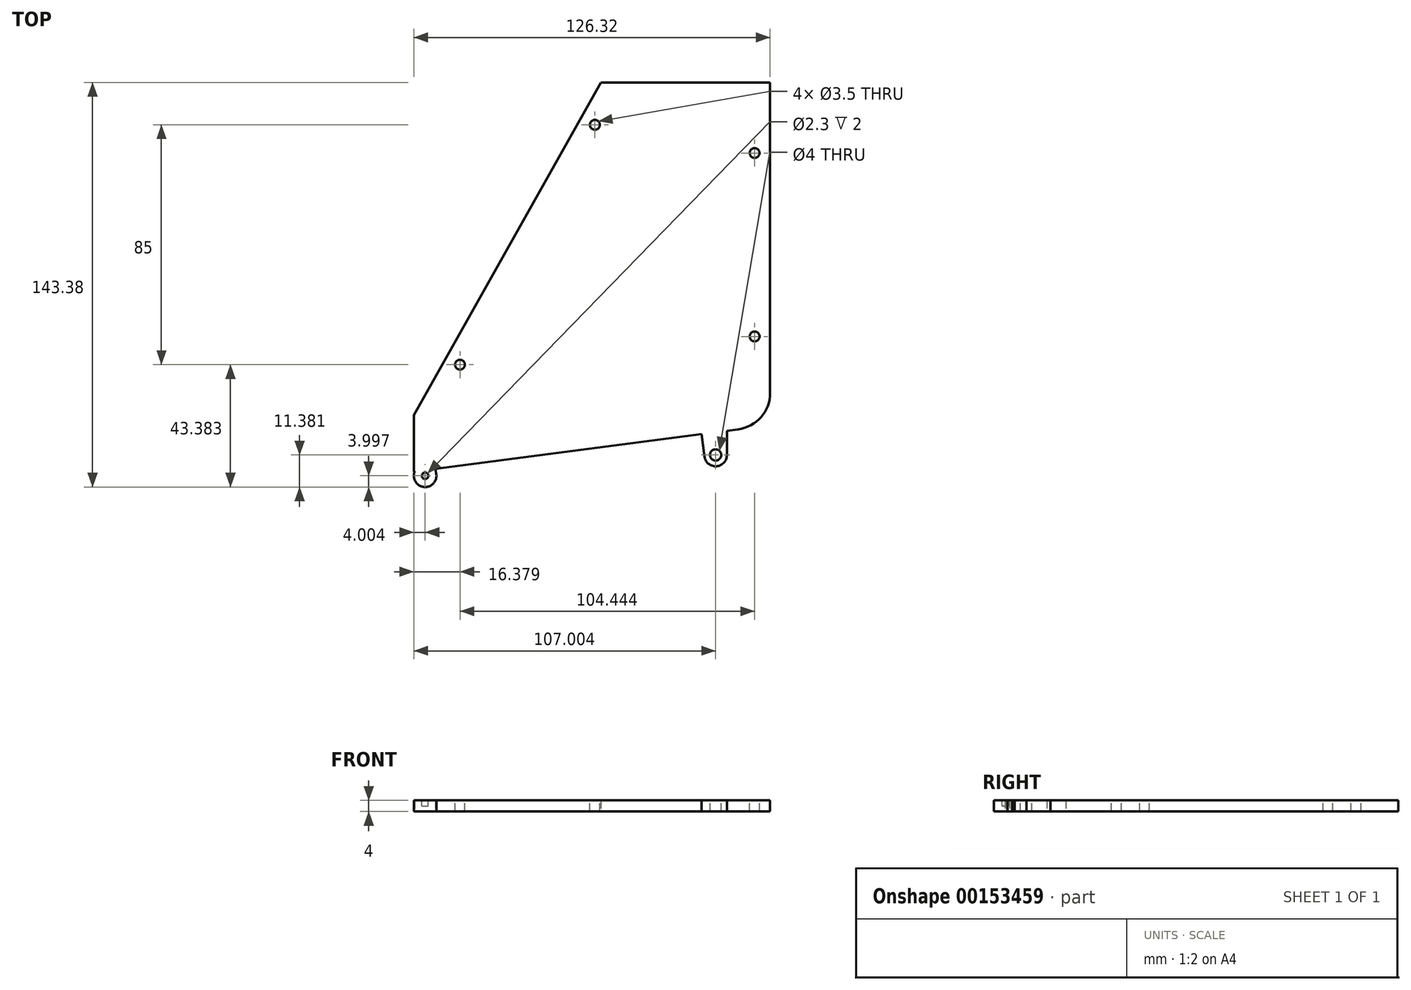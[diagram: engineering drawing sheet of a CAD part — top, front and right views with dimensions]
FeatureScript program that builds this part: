
annotation { "Feature Type Name" : "Feature", "Feature Type Description" : "" }
export const myFeature = defineFeature(function(context is Context, id is Id, definition is map)
    precondition{}
    {
        {
            var Q0;
            Q0=qCreatedBy(makeId("Top.planeOp"),FACE);
            var sketch = newSketch(context, id + "F0", { "sketchPlane" : qUnion([Q0])});
            skLineSegment(sketch, "E0", {"start": v(-60.03, 83.64) * mm, "end": v(-60.03, -26.36) * mm});
            skLineSegment(sketch, "E1", {"start": v(-48.72, -39.25) * mm, "end": v(66.28, -54.25) * mm});
            skLineSegment(sketch, "E2", {"start": v(66.28, -34.25) * mm, "end": v(-0.03, 83.64) * mm});
            skLineSegment(sketch, "E3", {"start": v(-60.03, 83.64) * mm, "end": v(-0.03, 83.64) * mm});
            skLineSegment(sketch, "E4", {"start": v(66.28, -34.25) * mm, "end": v(66.28, -54.25) * mm});
            skPoint(sketch, "E5.visualSharp", {"position": v(-60.03, -37.77) * mm});
            skArc(sketch, "E5.filletArc", {"start": v(-60.03, -26.36) * mm, "mid": v(-56.8, -34.93) * mm, "end": v(-48.72, -39.25) * mm});
            skCircle(sketch, "E6", {"center": v(62.28, -55.74) * mm, "radius": 4 * mm});
            skLineSegment(sketch, "E7", {"start": v(66.28, -55.79) * mm, "end": v(66.28, -54.25) * mm});
            skLineSegment(sketch, "E8", {"start": v(58.37, -54.91) * mm, "end": v(58.59, -53.24) * mm});
            skCircle(sketch, "E9", {"center": v(-40.72, -48.36) * mm, "radius": 4 * mm});
            skLineSegment(sketch, "E10", {"start": v(-44.71, -48.48) * mm, "end": v(-44.71, -39.77) * mm});
            skLineSegment(sketch, "E11", {"start": v(-36.75, -48.88) * mm, "end": v(-35.72, -40.94) * mm});
            skSolve(sketch);
        }
        {
            var Q0;
            {var subQ0=sQuery(id+"F0.wireOp",EDGE,"E7");var subQ1=sQuery(id+"F0.wireOp",EDGE,"E6");var subQ2=makeQuery(id+"F0.imprint","INTERSECT",VERTEX,{"disambiguationData":[OD(0.0)],"derivedFrom":[subQ1,subQ0]});Q0=makeQuery(id+"F0.imprint","IMPRINT",FACE,{"disambiguationData":[TD([[makeQuery(id+"F0.imprint","IMPRINT",EDGE,{"disambiguationData":[TD([[subQ2,-1.0]])],"derivedFrom":subQ1}),1.0]])]});}
            var Q1;
            {var subQ0=sQuery(id+"F0.wireOp",EDGE,"E10");var subQ1=sQuery(id+"F0.wireOp",EDGE,"E9");var subQ2=makeQuery(id+"F0.imprint","INTERSECT",VERTEX,{"disambiguationData":[OD(0.0)],"derivedFrom":[subQ1,subQ0]});Q1=makeQuery(id+"F0.imprint","IMPRINT",FACE,{"disambiguationData":[TD([[makeQuery(id+"F0.imprint","IMPRINT",EDGE,{"disambiguationData":[TD([[subQ2,1.0]])],"derivedFrom":subQ1}),1.0]])]});}
            var Q2;
            {var subQ0=sQuery(id+"F0.wireOp",EDGE,"E10");var subQ1=sQuery(id+"F0.wireOp",EDGE,"E1");var subQ2=makeQuery(id+"F0.imprint","INTERSECT",VERTEX,{"derivedFrom":[subQ1,subQ0]});Q2=makeQuery(id+"F0.imprint","IMPRINT",FACE,{"disambiguationData":[TD([[makeQuery(id+"F0.imprint","IMPRINT",EDGE,{"disambiguationData":[TD([[subQ2,-1.0]])],"derivedFrom":subQ1}),-1.0]])]});}
            var Q3;
            {var subQ0=sQuery(id+"F0.wireOp",EDGE,"E11");Q3=makeQuery(id+"F0.imprint","IMPRINT",FACE,{"disambiguationData":[TD([[makeQuery(id+"F0.imprint","IMPRINT",EDGE,{"derivedFrom":subQ0}),1.0]])]});}
            var Q4;
            {var subQ0=sQuery(id+"F0.wireOp",EDGE,"E8");Q4=makeQuery(id+"F0.imprint","IMPRINT",FACE,{"disambiguationData":[TD([[makeQuery(id+"F0.imprint","IMPRINT",EDGE,{"derivedFrom":subQ0}),-1.0]])]});}
            var Q5;
            {var subQ0=sQuery(id+"F0.wireOp",EDGE,"E7");var subQ3=sQuery(id+"F0.wireOp",EDGE,"E6");var subQ5=makeQuery(id+"F0.imprint","INTERSECT",VERTEX,{"disambiguationData":[OD(1.0)],"derivedFrom":[subQ3,subQ0]});Q5=makeQuery(id+"F0.imprint","IMPRINT",FACE,{"disambiguationData":[TD([[makeQuery(id+"F0.imprint","IMPRINT",EDGE,{"disambiguationData":[TD([[subQ5,-1.0]])],"derivedFrom":subQ3}),-1.0]])]});}
            var Q6;
            {var subQ0=sQuery(id+"F0.wireOp",EDGE,"E9");var subQ2=sQuery(id+"F0.wireOp",EDGE,"E1");var subQ7=makeQuery(id+"F0.imprint","INTERSECT",VERTEX,{"disambiguationData":[OD(0.0)],"derivedFrom":[subQ2,subQ0]});Q6=makeQuery(id+"F0.imprint","IMPRINT",FACE,{"disambiguationData":[TD([[makeQuery(id+"F0.imprint","IMPRINT",EDGE,{"disambiguationData":[TD([[subQ7,-1.0]])],"derivedFrom":subQ2}),-1.0]])]});}
            var Q7;
            {var subQ1=sQuery(id+"F0.wireOp",EDGE,"E6");var subQ4=sQuery(id+"F0.wireOp",EDGE,"E1");var subQ5=makeQuery(id+"F0.imprint","INTERSECT",VERTEX,{"disambiguationData":[OD(0.0)],"derivedFrom":[subQ4,subQ1]});Q7=makeQuery(id+"F0.imprint","IMPRINT",FACE,{"disambiguationData":[TD([[makeQuery(id+"F0.imprint","IMPRINT",EDGE,{"disambiguationData":[TD([[subQ5,-1.0]])],"derivedFrom":subQ4}),-1.0]])]});}
            var Q8;
            {var subQ0=sQuery(id+"F0.wireOp",EDGE,"E6");var subQ1=sQuery(id+"F0.wireOp",EDGE,"E1");var subQ2=makeQuery(id+"F0.imprint","INTERSECT",VERTEX,{"disambiguationData":[OD(0.0)],"derivedFrom":[subQ1,subQ0]});Q8=makeQuery(id+"F0.imprint","IMPRINT",FACE,{"disambiguationData":[TD([[makeQuery(id+"F0.imprint","IMPRINT",EDGE,{"disambiguationData":[TD([[subQ2,-1.0]])],"derivedFrom":subQ1}),1.0]])]});}
            var Q9;
            Q9=makeQuery(id+"F0.imprint","IMPRINT",FACE,{"disambiguationData":[TD([[makeQuery(id+"F0.imprint","IMPRINT",EDGE,{"derivedFrom":sQuery(id+"F0.wireOp",EDGE,"E0")}),1.0]])]});
            var Q10;
            {var subQ0=sQuery(id+"F0.wireOp",EDGE,"E9");var subQ1=sQuery(id+"F0.wireOp",EDGE,"E1");var subQ2=makeQuery(id+"F0.imprint","INTERSECT",VERTEX,{"disambiguationData":[OD(0.0)],"derivedFrom":[subQ1,subQ0]});Q10=makeQuery(id+"F0.imprint","IMPRINT",FACE,{"disambiguationData":[TD([[makeQuery(id+"F0.imprint","IMPRINT",EDGE,{"disambiguationData":[TD([[subQ2,-1.0]])],"derivedFrom":subQ1}),1.0]])]});}
            var Q11;
            {var subQ0=sQuery(id+"F0.wireOp",EDGE,"E10");var subQ1=sQuery(id+"F0.wireOp",EDGE,"E9");var subQ2=makeQuery(id+"F0.imprint","INTERSECT",VERTEX,{"disambiguationData":[OD(0.0)],"derivedFrom":[subQ1,subQ0]});Q11=makeQuery(id+"F0.imprint","IMPRINT",FACE,{"disambiguationData":[TD([[makeQuery(id+"F0.imprint","IMPRINT",EDGE,{"disambiguationData":[TD([[subQ2,-1.0]])],"derivedFrom":subQ1}),1.0]])]});}
            extrude(context, id + "F1", {"entities" : qUnion([Q0, Q1, Q2, Q3, Q4, Q5, Q6, Q7, Q8, Q9, Q10, Q11]), "depth" : 4 * mm});
        }
        {
            var Q0;
            Q0=makeQuery(id+"F1.opExtrude","CAP_FACE",FACE,{"disambiguationData":[OSD([sQuery(id+"F0.wireOp",EDGE,"E0"),sQuery(id+"F0.wireOp",EDGE,"E1"),sQuery(id+"F0.wireOp",EDGE,"E2"),sQuery(id+"F0.wireOp",EDGE,"E3"),sQuery(id+"F0.wireOp",EDGE,"E4"),sQuery(id+"F0.wireOp",EDGE,"E5.filletArc")])],"isStart":false});
            var sketch = newSketch(context, id + "F2", { "sketchPlane" : qUnion([Q0])});
            skLineSegment(sketch, "E12.0", {"start": v(-48.46, -37.26) * mm, "end": v(52.4, -50.42) * mm});
            skArc(sketch, "E12.1", {"start": v(-58.03, -26.36) * mm, "mid": v(-55.3, -33.61) * mm, "end": v(-48.46, -37.26) * mm});
            skLineSegment(sketch, "E12.2", {"start": v(-58.03, 83.64) * mm, "end": v(-58.03, -26.36) * mm});
            skLineSegment(sketch, "E13", {"start": v(66.28, -54.25) * mm, "end": v(66.28, -52.23) * mm});
            skLineSegment(sketch, "E14", {"start": v(-60.03, 83.64) * mm, "end": v(-58.03, 83.64) * mm});
            skLineSegment(sketch, "E15", {"start": v(-48.46, -37.26) * mm, "end": v(-48.72, -39.25) * mm});
            skLineSegment(sketch, "E16.0", {"start": v(59.2, -25.73) * mm, "end": v(-2.7, 84.31) * mm});
            skLineSegment(sketch, "E17", {"start": v(-2.33, 83.64) * mm, "end": v(-2.7, 84.31) * mm});
            skLineSegment(sketch, "E18", {"start": v(59.2, -25.73) * mm, "end": v(66.28, -34.25) * mm});
            skSolve(sketch);
        }
        {
            var Q0;
            Q0=qSketchRegion(id+"F2",true);
            var Q1;
            Q1=makeQuery(id+"F2.imprint","IMPRINT",FACE,{"disambiguationData":[TD([[makeQuery(id+"F2.imprint","IMPRINT",EDGE,{"derivedFrom":sQuery(id+"F2.wireOp",EDGE,"E12.1")}),-1.0]])]});
            var Q2;
            {var subQ2=sQuery(id+"F2.wireOp",EDGE,"E17");Q2=makeQuery(id+"F2.imprint","IMPRINT",FACE,{"disambiguationData":[TD([[makeQuery(id+"F2.imprint","IMPRINT",EDGE,{"derivedFrom":subQ2}),-1.0]])]});}
            var Q3;
            {var subQ0=sQuery(id+"F2.wireOp",EDGE,"E16.0");Q3=makeQuery(id+"F2.imprint","IMPRINT",FACE,{"disambiguationData":[TD([[makeQuery(id+"F2.imprint","IMPRINT",EDGE,{"derivedFrom":subQ0}),-1.0]])]});}
            extrude(context, id + "F3", {"entities" : qUnion([Q0, Q1, Q2, Q3]), "operationType" : NewBodyOperationType.ADD, "depth" : 55 * mm});
        }
        {
            var Q0;
            {var subQ0=sQuery(id+"F0.wireOp",EDGE,"E0");Q0=makeQuery(id+"F3.boolean.opBoolean","MERGE",FACE,{"derivedFrom":[makeQuery(id+"F1.opExtrude","SWEPT_FACE",FACE,{"disambiguationData":[OSD([subQ0])]}),makeQuery(id+"F3.opExtrude","SWEPT_FACE",FACE,{"disambiguationData":[OSD([subQ0])]})]});}
            var sketch = newSketch(context, id + "F4", { "sketchPlane" : qUnion([Q0])});
            skCircle(sketch, "E19", {"center": v(23.36, 41.5) * mm, "radius": 2.5 * mm});
            skCircle(sketch, "E20", {"center": v(-74.64, 41.5) * mm, "radius": 2.5 * mm});
            skSolve(sketch);
        }
        {
            var Q0;
            Q0=qSketchRegion(id+"F4",true);
            extrude(context, id + "F5", {"entities" : qUnion([Q0]), "operationType" : NewBodyOperationType.REMOVE, "endBound" : BoundingType.UP_TO_NEXT, "oppositeDirection" : true, "depth" : 25 * mm});
        }
        {
            var Q0;
            Q0=makeQuery(id+"F1.opExtrude","CAP_FACE",FACE,{"disambiguationData":[OSD([sQuery(id+"F0.wireOp",EDGE,"E0"),sQuery(id+"F0.wireOp",EDGE,"E1"),sQuery(id+"F0.wireOp",EDGE,"E2"),sQuery(id+"F0.wireOp",EDGE,"E3"),sQuery(id+"F0.wireOp",EDGE,"E4"),sQuery(id+"F0.wireOp",EDGE,"E5.filletArc"),sQuery(id+"F0.wireOp",EDGE,"E6"),sQuery(id+"F0.wireOp",EDGE,"E7"),sQuery(id+"F0.wireOp",EDGE,"E8")])],"isStart":false});
            var sketch = newSketch(context, id + "F6", { "sketchPlane" : qUnion([Q0])});
            skCircle(sketch, "E21", {"center": v(62.28, -55.74) * mm, "radius": 1.15 * mm});
            skSolve(sketch);
        }
        {
            var Q0;
            Q0=qSketchRegion(id+"F6",true);
            extrude(context, id + "F7", {"entities" : qUnion([Q0]), "operationType" : NewBodyOperationType.REMOVE, "oppositeDirection" : true, "depth" : 2 * mm});
        }
        {
            var Q0;
            Q0=makeQuery(id+"F3.opExtrude","CAP_FACE",FACE,{"disambiguationData":[OSD([sQuery(id+"F0.wireOp",EDGE,"E0"),sQuery(id+"F0.wireOp",EDGE,"E5.filletArc"),sQuery(id+"F2.wireOp",EDGE,"E12.1"),sQuery(id+"F2.wireOp",EDGE,"E12.2"),sQuery(id+"F2.wireOp",EDGE,"E14"),sQuery(id+"F2.wireOp",EDGE,"E15")])],"isStart":false});
            var sketch = newSketch(context, id + "F8", { "sketchPlane" : qUnion([Q0])});
            skCircle(sketch, "E22", {"center": v(-54.53, -6.36) * mm, "radius": 3.5 * mm});
            skLineSegment(sketch, "E23", {"start": v(-51.48, -4.64) * mm, "end": v(-58.03, 5.64) * mm});
            skLineSegment(sketch, "E24", {"start": v(-52.77, -9.38) * mm, "end": v(-58.03, -12.36) * mm});
            skCircle(sketch, "E25", {"center": v(-54.53, 58.64) * mm, "radius": 3.5 * mm});
            skLineSegment(sketch, "E26", {"start": v(-51.64, 60.61) * mm, "end": v(-58.03, 70.64) * mm});
            skLineSegment(sketch, "E27", {"start": v(-53.23, 55.4) * mm, "end": v(-58.03, 53.64) * mm});
            skSolve(sketch);
        }
        {
            var Q0;
            Q0=qSketchRegion(id+"F8",true);
            var Q1;
            {var subQ0=sQuery(id+"F8.wireOp",EDGE,"E23");Q1=makeQuery(id+"F8.imprint","IMPRINT",FACE,{"disambiguationData":[TD([[makeQuery(id+"F8.imprint","IMPRINT",EDGE,{"derivedFrom":subQ0}),1.0]])]});}
            var Q2;
            {var subQ0=sQuery(id+"F8.wireOp",EDGE,"E24");Q2=makeQuery(id+"F8.imprint","IMPRINT",FACE,{"disambiguationData":[TD([[makeQuery(id+"F8.imprint","IMPRINT",EDGE,{"derivedFrom":subQ0}),-1.0]])]});}
            var Q3;
            {var subQ0=sQuery(id+"F8.wireOp",EDGE,"E26");Q3=makeQuery(id+"F8.imprint","IMPRINT",FACE,{"disambiguationData":[TD([[makeQuery(id+"F8.imprint","IMPRINT",EDGE,{"derivedFrom":subQ0}),1.0]])]});}
            var Q4;
            {var subQ0=sQuery(id+"F8.wireOp",EDGE,"E27");var subQ1=sQuery(id+"F8.wireOp",EDGE,"E25");var subQ2=makeQuery(id+"F8.imprint","INTERSECT",VERTEX,{"disambiguationData":[OD(1.0)],"derivedFrom":[subQ1,subQ0]});Q4=makeQuery(id+"F8.imprint","IMPRINT",FACE,{"disambiguationData":[TD([[makeQuery(id+"F8.imprint","IMPRINT",EDGE,{"disambiguationData":[TD([[subQ2,1.0]])],"derivedFrom":subQ1}),-1.0]])]});}
            extrude(context, id + "F9", {"entities" : qUnion([Q0, Q1, Q2, Q3, Q4]), "operationType" : NewBodyOperationType.ADD, "oppositeDirection" : true, "depth" : 8 * mm});
        }
        {
            var Q0;
            Q0=makeQuery(id+"F3.opExtrude","CAP_FACE",FACE,{"disambiguationData":[OSD([sQuery(id+"F0.wireOp",EDGE,"E2"),sQuery(id+"F0.wireOp",EDGE,"E3"),sQuery(id+"F2.wireOp",EDGE,"E16.0"),sQuery(id+"F2.wireOp",EDGE,"E18")])],"isStart":false});
            var sketch = newSketch(context, id + "F10", { "sketchPlane" : qUnion([Q0])});
            skCircle(sketch, "E28", {"center": v(2.1, 68.64) * mm, "radius": 3.5 * mm});
            skLineSegment(sketch, "E29", {"start": v(-1.4, 68.87) * mm, "end": v(-0.64, 80.64) * mm});
            skLineSegment(sketch, "E30", {"start": v(1.24, 65.25) * mm, "end": v(8.92, 63.64) * mm});
            skCircle(sketch, "E31", {"center": v(49.9, -16.36) * mm, "radius": 3.5 * mm});
            skLineSegment(sketch, "E32", {"start": v(46.47, -15.72) * mm, "end": v(47.17, -4.36) * mm});
            skLineSegment(sketch, "E33", {"start": v(49.2, -19.78) * mm, "end": v(56.74, -21.36) * mm});
            skSolve(sketch);
        }
        {
            var Q0;
            {var subQ0=sQuery(id+"F10.wireOp",EDGE,"E32");var subQ1=sQuery(id+"F10.wireOp",EDGE,"E31");var subQ2=makeQuery(id+"F10.imprint","INTERSECT",VERTEX,{"disambiguationData":[OD(1.0)],"derivedFrom":[subQ1,subQ0]});Q0=makeQuery(id+"F10.imprint","IMPRINT",FACE,{"disambiguationData":[TD([[makeQuery(id+"F10.imprint","IMPRINT",EDGE,{"disambiguationData":[TD([[subQ2,1.0]])],"derivedFrom":subQ1}),1.0]])]});}
            var Q1;
            {var subQ0=sQuery(id+"F10.wireOp",EDGE,"E32");var subQ1=sQuery(id+"F10.wireOp",EDGE,"E31");var subQ2=makeQuery(id+"F10.imprint","INTERSECT",VERTEX,{"disambiguationData":[OD(1.0)],"derivedFrom":[subQ1,subQ0]});Q1=makeQuery(id+"F10.imprint","IMPRINT",FACE,{"disambiguationData":[TD([[makeQuery(id+"F10.imprint","IMPRINT",EDGE,{"disambiguationData":[TD([[subQ2,1.0]])],"derivedFrom":subQ1}),-1.0]])]});}
            var Q2;
            {var subQ0=sQuery(id+"F10.wireOp",EDGE,"E33");Q2=makeQuery(id+"F10.imprint","IMPRINT",FACE,{"disambiguationData":[TD([[makeQuery(id+"F10.imprint","IMPRINT",EDGE,{"derivedFrom":subQ0}),1.0]])]});}
            var Q3;
            {var subQ0=sQuery(id+"F10.wireOp",EDGE,"E28");var subQ1=makeQuery(id+"F10.imprint","INTERSECT",VERTEX,{"derivedFrom":[subQ0,sQuery(id+"F10.wireOp",EDGE,"E29")]});Q3=makeQuery(id+"F10.imprint","IMPRINT",FACE,{"disambiguationData":[TD([[makeQuery(id+"F10.imprint","IMPRINT",EDGE,{"disambiguationData":[TD([[subQ1,1.0]])],"derivedFrom":subQ0}),1.0]])]});}
            var Q4;
            {var subQ0=sQuery(id+"F10.wireOp",EDGE,"E30");var subQ1=sQuery(id+"F10.wireOp",EDGE,"E28");var subQ2=makeQuery(id+"F10.imprint","INTERSECT",VERTEX,{"disambiguationData":[OD(1.0)],"derivedFrom":[subQ1,subQ0]});Q4=makeQuery(id+"F10.imprint","IMPRINT",FACE,{"disambiguationData":[TD([[makeQuery(id+"F10.imprint","IMPRINT",EDGE,{"disambiguationData":[TD([[subQ2,-1.0]])],"derivedFrom":subQ1}),-1.0]])]});}
            var Q5;
            {var subQ0=sQuery(id+"F10.wireOp",EDGE,"E29");Q5=makeQuery(id+"F10.imprint","IMPRINT",FACE,{"disambiguationData":[TD([[makeQuery(id+"F10.imprint","IMPRINT",EDGE,{"derivedFrom":subQ0}),-1.0]])]});}
            extrude(context, id + "F11", {"entities" : qUnion([Q0, Q1, Q2, Q3, Q4, Q5]), "operationType" : NewBodyOperationType.ADD, "oppositeDirection" : true, "depth" : 7 * mm});
        }
        {
            var Q0;
            {var subQ0=sQuery(id+"F2.wireOp",EDGE,"E12.2");Q0=makeQuery(id+"F9.boolean.opBoolean","MERGE",FACE,{"derivedFrom":[makeQuery(id+"F3.opExtrude","CAP_FACE",FACE,{"disambiguationData":[OSD([sQuery(id+"F0.wireOp",EDGE,"E0"),sQuery(id+"F0.wireOp",EDGE,"E5.filletArc"),sQuery(id+"F2.wireOp",EDGE,"E12.1"),subQ0,sQuery(id+"F2.wireOp",EDGE,"E14"),sQuery(id+"F2.wireOp",EDGE,"E15")])],"isStart":false}),makeQuery(id+"F9.opExtrude","CAP_FACE",FACE,{"disambiguationData":[OSD([subQ0,sQuery(id+"F8.wireOp",EDGE,"E22"),sQuery(id+"F8.wireOp",EDGE,"E23"),sQuery(id+"F8.wireOp",EDGE,"E24")])],"isStart":true}),makeQuery(id+"F9.opExtrude","CAP_FACE",FACE,{"disambiguationData":[OSD([subQ0,sQuery(id+"F8.wireOp",EDGE,"E25"),sQuery(id+"F8.wireOp",EDGE,"E26"),sQuery(id+"F8.wireOp",EDGE,"E27")])],"isStart":true})]});}
            var sketch = newSketch(context, id + "F12", { "sketchPlane" : qUnion([Q0])});
            skCircle(sketch, "E34", {"center": v(-54.53, -6.36) * mm, "radius": 1.75 * mm});
            skCircle(sketch, "E35", {"center": v(-54.53, 58.64) * mm, "radius": 1.75 * mm});
            skSolve(sketch);
        }
        {
            var Q0;
            Q0=qSketchRegion(id+"F12",true);
            extrude(context, id + "F13", {"entities" : qUnion([Q0]), "operationType" : NewBodyOperationType.REMOVE, "endBound" : BoundingType.THROUGH_ALL, "oppositeDirection" : true, "depth" : 6.5 * mm});
        }
        {
            var Q0;
            {var subQ0=sQuery(id+"F2.wireOp",EDGE,"E16.0");Q0=makeQuery(id+"F11.boolean.opBoolean","MERGE",FACE,{"derivedFrom":[makeQuery(id+"F3.opExtrude","CAP_FACE",FACE,{"disambiguationData":[OSD([sQuery(id+"F0.wireOp",EDGE,"E2"),sQuery(id+"F0.wireOp",EDGE,"E3"),subQ0,sQuery(id+"F2.wireOp",EDGE,"E18")])],"isStart":false}),makeQuery(id+"F11.opExtrude","CAP_FACE",FACE,{"disambiguationData":[OSD([subQ0,sQuery(id+"F10.wireOp",EDGE,"E28"),sQuery(id+"F10.wireOp",EDGE,"E29"),sQuery(id+"F10.wireOp",EDGE,"E30")])],"isStart":true}),makeQuery(id+"F11.opExtrude","CAP_FACE",FACE,{"disambiguationData":[OSD([subQ0,sQuery(id+"F10.wireOp",EDGE,"E31"),sQuery(id+"F10.wireOp",EDGE,"E32"),sQuery(id+"F10.wireOp",EDGE,"E33")])],"isStart":true})]});}
            var sketch = newSketch(context, id + "F14", { "sketchPlane" : qUnion([Q0])});
            skCircle(sketch, "E36", {"center": v(49.9, -16.36) * mm, "radius": 1.75 * mm});
            skCircle(sketch, "E37", {"center": v(2.1, 68.64) * mm, "radius": 1.75 * mm});
            skSolve(sketch);
        }
        {
            var Q0;
            Q0=qSketchRegion(id+"F14",true);
            extrude(context, id + "F15", {"entities" : qUnion([Q0]), "operationType" : NewBodyOperationType.REMOVE, "endBound" : BoundingType.THROUGH_ALL, "oppositeDirection" : true, "depth" : 6.5 * mm});
        }
        {
            var Q0;
            {var subQ0=sQuery(id+"F2.wireOp",EDGE,"E12.2");Q0=makeQuery(id+"F9.boolean.opBoolean","MERGE",FACE,{"derivedFrom":[makeQuery(id+"F3.opExtrude","CAP_FACE",FACE,{"disambiguationData":[OSD([sQuery(id+"F0.wireOp",EDGE,"E0"),sQuery(id+"F0.wireOp",EDGE,"E5.filletArc"),sQuery(id+"F2.wireOp",EDGE,"E12.1"),subQ0,sQuery(id+"F2.wireOp",EDGE,"E14"),sQuery(id+"F2.wireOp",EDGE,"E15")])],"isStart":false}),makeQuery(id+"F9.opExtrude","CAP_FACE",FACE,{"disambiguationData":[OSD([subQ0,sQuery(id+"F8.wireOp",EDGE,"E22"),sQuery(id+"F8.wireOp",EDGE,"E23"),sQuery(id+"F8.wireOp",EDGE,"E24")])],"isStart":true}),makeQuery(id+"F9.opExtrude","CAP_FACE",FACE,{"disambiguationData":[OSD([subQ0,sQuery(id+"F8.wireOp",EDGE,"E25"),sQuery(id+"F8.wireOp",EDGE,"E26"),sQuery(id+"F8.wireOp",EDGE,"E27")])],"isStart":true})]});}
            extrude(context, id + "F16", {"entities" : qUnion([Q0]), "operationType" : NewBodyOperationType.REMOVE, "oppositeDirection" : true, "depth" : 55 * mm});
        }
        {
            var Q0;
            {var subQ0=sQuery(id+"F2.wireOp",EDGE,"E16.0");Q0=makeQuery(id+"F11.boolean.opBoolean","MERGE",FACE,{"derivedFrom":[makeQuery(id+"F3.opExtrude","CAP_FACE",FACE,{"disambiguationData":[OSD([sQuery(id+"F0.wireOp",EDGE,"E2"),sQuery(id+"F0.wireOp",EDGE,"E3"),subQ0,sQuery(id+"F2.wireOp",EDGE,"E18")])],"isStart":false}),makeQuery(id+"F11.opExtrude","CAP_FACE",FACE,{"disambiguationData":[OSD([subQ0,sQuery(id+"F10.wireOp",EDGE,"E28"),sQuery(id+"F10.wireOp",EDGE,"E29"),sQuery(id+"F10.wireOp",EDGE,"E30")])],"isStart":true}),makeQuery(id+"F11.opExtrude","CAP_FACE",FACE,{"disambiguationData":[OSD([subQ0,sQuery(id+"F10.wireOp",EDGE,"E31"),sQuery(id+"F10.wireOp",EDGE,"E32"),sQuery(id+"F10.wireOp",EDGE,"E33")])],"isStart":true})]});}
            var Q1;
            {var subQ0=sQuery(id+"F0.wireOp",EDGE,"E5.filletArc");var subQ1=sQuery(id+"F0.wireOp",EDGE,"E0");Q1=makeQuery(id+"F16.boolean.opBoolean","MERGE",FACE,{"derivedFrom":[makeQuery(id+"F1.opExtrude","CAP_FACE",FACE,{"disambiguationData":[OSD([subQ1,sQuery(id+"F0.wireOp",EDGE,"E1"),sQuery(id+"F0.wireOp",EDGE,"E2"),sQuery(id+"F0.wireOp",EDGE,"E3"),sQuery(id+"F0.wireOp",EDGE,"E4"),subQ0,sQuery(id+"F0.wireOp",EDGE,"E6"),sQuery(id+"F0.wireOp",EDGE,"E7"),sQuery(id+"F0.wireOp",EDGE,"E8"),sQuery(id+"F0.wireOp",EDGE,"E9"),sQuery(id+"F0.wireOp",EDGE,"E10"),sQuery(id+"F0.wireOp",EDGE,"E11")])],"isStart":false}),makeQuery(id+"F16.opExtrude","CAP_FACE",FACE,{"disambiguationData":[OSD([subQ1,subQ0,sQuery(id+"F2.wireOp",EDGE,"E12.1"),sQuery(id+"F2.wireOp",EDGE,"E12.2"),sQuery(id+"F2.wireOp",EDGE,"E14"),sQuery(id+"F2.wireOp",EDGE,"E15"),sQuery(id+"F8.wireOp",EDGE,"E22"),sQuery(id+"F8.wireOp",EDGE,"E23"),sQuery(id+"F8.wireOp",EDGE,"E24"),sQuery(id+"F8.wireOp",EDGE,"E25"),sQuery(id+"F8.wireOp",EDGE,"E26"),sQuery(id+"F8.wireOp",EDGE,"E27")])],"isStart":false})]});}
            extrude(context, id + "F17", {"entities" : qUnion([Q0]), "operationType" : NewBodyOperationType.REMOVE, "endBound" : BoundingType.UP_TO_SURFACE, "oppositeDirection" : true, "endBoundEntityFace" : qUnion([Q1]), "depth" : 55 * mm});
        }
        {
            var Q0;
            Q0=makeQuery(id+"F1.opExtrude","SWEPT_BODY",BODY,{"disambiguationData":[OSD([sQuery(id+"F0.wireOp",EDGE,"E0"),sQuery(id+"F0.wireOp",EDGE,"E1"),sQuery(id+"F0.wireOp",EDGE,"E2"),sQuery(id+"F0.wireOp",EDGE,"E3"),sQuery(id+"F0.wireOp",EDGE,"E4"),sQuery(id+"F0.wireOp",EDGE,"E5.filletArc"),sQuery(id+"F0.wireOp",EDGE,"E6"),sQuery(id+"F0.wireOp",EDGE,"E7"),sQuery(id+"F0.wireOp",EDGE,"E8"),sQuery(id+"F0.wireOp",EDGE,"E9"),sQuery(id+"F0.wireOp",EDGE,"E10"),sQuery(id+"F0.wireOp",EDGE,"E11")])]});
            var Q1;
            Q1=makeQuery(id+"F1.opExtrude","SWEPT_FACE",FACE,{"disambiguationData":[OSD([sQuery(id+"F0.wireOp",EDGE,"E4")])]});
            mirror(context, id + "F18", {"entities" : qUnion([Q0]), "mirrorPlane" : qUnion([Q1])});
        }
        {
            var Q0;
            Q0=makeQuery(id+"F1.opExtrude","SWEPT_BODY",BODY,{"disambiguationData":[OSD([sQuery(id+"F0.wireOp",EDGE,"E0"),sQuery(id+"F0.wireOp",EDGE,"E1"),sQuery(id+"F0.wireOp",EDGE,"E2"),sQuery(id+"F0.wireOp",EDGE,"E3"),sQuery(id+"F0.wireOp",EDGE,"E4"),sQuery(id+"F0.wireOp",EDGE,"E5.filletArc"),sQuery(id+"F0.wireOp",EDGE,"E6"),sQuery(id+"F0.wireOp",EDGE,"E7"),sQuery(id+"F0.wireOp",EDGE,"E8"),sQuery(id+"F0.wireOp",EDGE,"E9"),sQuery(id+"F0.wireOp",EDGE,"E10"),sQuery(id+"F0.wireOp",EDGE,"E11")])]});
            deleteBodies(context, id + "F19", {"entities" : qUnion([Q0])});
        }
        {
            var Q0;
            {var subQ0=sQuery(id+"F8.wireOp",EDGE,"E27");var subQ1=sQuery(id+"F8.wireOp",EDGE,"E26");var subQ2=sQuery(id+"F8.wireOp",EDGE,"E25");var subQ3=sQuery(id+"F8.wireOp",EDGE,"E24");var subQ4=sQuery(id+"F8.wireOp",EDGE,"E23");var subQ5=sQuery(id+"F8.wireOp",EDGE,"E22");var subQ6=sQuery(id+"F2.wireOp",EDGE,"E15");var subQ7=sQuery(id+"F2.wireOp",EDGE,"E14");var subQ8=sQuery(id+"F2.wireOp",EDGE,"E12.2");var subQ9=sQuery(id+"F2.wireOp",EDGE,"E12.1");var subQ10=sQuery(id+"F0.wireOp",EDGE,"E11");var subQ11=sQuery(id+"F0.wireOp",EDGE,"E10");var subQ12=sQuery(id+"F0.wireOp",EDGE,"E9");var subQ13=sQuery(id+"F0.wireOp",EDGE,"E8");var subQ14=sQuery(id+"F0.wireOp",EDGE,"E7");var subQ15=sQuery(id+"F0.wireOp",EDGE,"E6");var subQ16=sQuery(id+"F0.wireOp",EDGE,"E5.filletArc");var subQ17=sQuery(id+"F0.wireOp",EDGE,"E4");var subQ18=sQuery(id+"F0.wireOp",EDGE,"E3");var subQ19=sQuery(id+"F0.wireOp",EDGE,"E2");var subQ20=sQuery(id+"F0.wireOp",EDGE,"E1");var subQ21=sQuery(id+"F0.wireOp",EDGE,"E0");Q0=makeQuery(id+"F18.opPattern","COPY",FACE,{"derivedFrom":makeQuery(id+"F17.boolean.opBoolean","MERGE",FACE,{"derivedFrom":[makeQuery(id+"F16.boolean.opBoolean","MERGE",FACE,{"derivedFrom":[makeQuery(id+"F1.opExtrude","CAP_FACE",FACE,{"disambiguationData":[OSD([subQ21,subQ20,subQ19,subQ18,subQ17,subQ16,subQ15,subQ14,subQ13,subQ12,subQ11,subQ10])],"isStart":false}),makeQuery(id+"F16.opExtrude","CAP_FACE",FACE,{"disambiguationData":[OSD([subQ21,subQ16,subQ9,subQ8,subQ7,subQ6,subQ5,subQ4,subQ3,subQ2,subQ1,subQ0])],"isStart":false})]}),makeQuery(id+"F17.opExtrude","CAP_FACE",FACE,{"disambiguationData":[OSD([subQ21,subQ20,subQ19,subQ18,subQ17,subQ16,subQ15,subQ14,subQ13,subQ12,subQ11,subQ10,subQ9,subQ8,subQ7,subQ6,subQ5,subQ4,subQ3,subQ2,subQ1,subQ0])],"isStart":false})]}),"instanceName":"1"});}
            var sketch = newSketch(context, id + "F20", { "sketchPlane" : qUnion([Q0])});
            skCircle(sketch, "E38", {"center": v(173.28, -48.36) * mm, "radius": 2 * mm});
            skSolve(sketch);
        }
        {
            var Q0;
            Q0 = qSketchRegion(id + "F20", true);
            extrude(context, id + "F21", {"entities" : qUnion([Q0]), "operationType" : NewBodyOperationType.REMOVE, "endBound" : BoundingType.UP_TO_NEXT, "oppositeDirection" : true, "depth" : 25 * mm});
        }
    });
